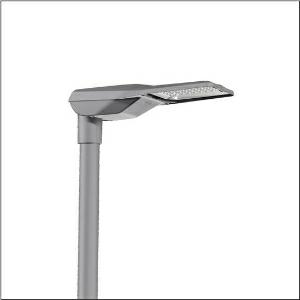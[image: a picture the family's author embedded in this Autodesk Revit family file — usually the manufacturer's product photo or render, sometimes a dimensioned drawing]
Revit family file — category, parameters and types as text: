
# Revit family: streetlight_sl_21_iq_mini___stw1_0a_5xe2e41d08jb_35ba
name_source: partatom
category: Lighting Fixtures
units: mm (PartAtom-declared; Revit-internal decimal feet)

## family parameters
Cut with Voids When Loaded = No
Host = Face
Light Source = No
Part Type = Normal
Room Calculation Point = No
Round Connector Dimension = Use Diameter
Shared = No

## types (1)
- --- (1 x LED, 11290 lm, 71.6 W, 4000K)
    Apparent Load = 72 VA
    CIE Flux Codes = 39 75 98 100 100
    Color Rendering = 70
    Color Temperature = 4000K
    Default Elevation = 1800 mm
    Description = Streetlight SL 21 iQ mini, mast luminaire, primary light control with lens, of PMMA, primary optical cover: cover, of toughened safety glass, transparent, light distribution: STW1.0a, light emission: direct distribution, primary light characteristic: asymmetric, installation type: post-top, side-entry, LED, High Power LED, rated luminous flux: 11.290lm, luminous efficacy: 158lm/W, light colour: 740, colour temperature: 4000K, control gear: iQ-Comfort, control: Auto-Match, Temp-Guard, Lumen-Switch, Night-Set, Smart-Wire, Light-Fading, Desk-Remote (wireless, voltage-free reading and setting of iQ features in the workshop via application-optimized NFC function/RFID function), optimised constant luminous flux control (CLO 2.0), pre-setting: linear dimming characteristic, mains connection: 220..240V, AC, 50/60Hz, start of lifetime: 72W, end of service life: 75W, reduction: 33W, luminaire housing, of diecast aluminium, powder-coated, Siteco® metallic grey (DB 702S), corrosivity category C5 mid according to DIN EN ISO 12944, please order mast flange separately, inclination adjustable: 0°, 5°, 10°, 15°, sealing non-destructively replaceable, multi-level sealing system, length: 628mm, width: 235mm, height: 110mm, mast flange for spigot size: 42mm (side-entry): 5XC10008XM4, 60/48mm (side-entry/post-top): 5XC10108XM2, 76/60mm (side-entry/post-top): 5XC10108XM1, mounting height: 4..8m, protection rating (complete): IP66, insulation class (complete): insulation class II (safety insulation), certification: CE, ENEC, ENEC+, VDE, impact resistance: IK10, permissible operating ambient temperature for outdoor applications: -40..+50°C, standard-compliant lighting for roads and squares, packaging unit: 1 piece

Light Distribution: STW1.0a
    Height = 110 mm
    Lamp = 1 x LED
    Lamp Light Flux = 11290 lm
    Lamp Power = 71.6 W
    Lamp count = 1
    Length = 625 mm
    Luminous efficacy = 158 lm/W
    Manufacturer = Siteco
    ModVariant = No
    Model = 5XE2E41D08JB
    Number of Poles = 1
    OnlyDefault = Yes
    Power Factor = 1
    Product Name = Streetlight SL 21 iQ mini | STW1.0a
    Product group = mast luminaire | pylon top
    ProductGroupID = 6100
    Protection Class = Protection class II
    Protection Degree = IP 66
    RLX_Detail_Level = 1
    RLX_Emergency_Light_Flux = 0 lm
    RLX_Emergency_Type = 0
    RLX_Emergency_Type_DB = No
    RlxData = <blob elided: 26413 chars, md5=bb9a723c>
    Socket = socket
    Standby Power = 0 W
    System Light Flux = 11290 lm
    System Power = 72 W
    Type Comments = factory setting: luminous flux: 100 % | dim-lin: 254 | 746 mA
    Type Image = l_1003519.jpg
    URL = http://relux.com
    VarID = @adj_191623
    Voltage = 0 V
    Weight = 0.00 kg
    Width = 234 mm

## geometry (parser evidence)
native form markers: Blend x4, Sweep x12
no freeform markers — native parametric forms only
